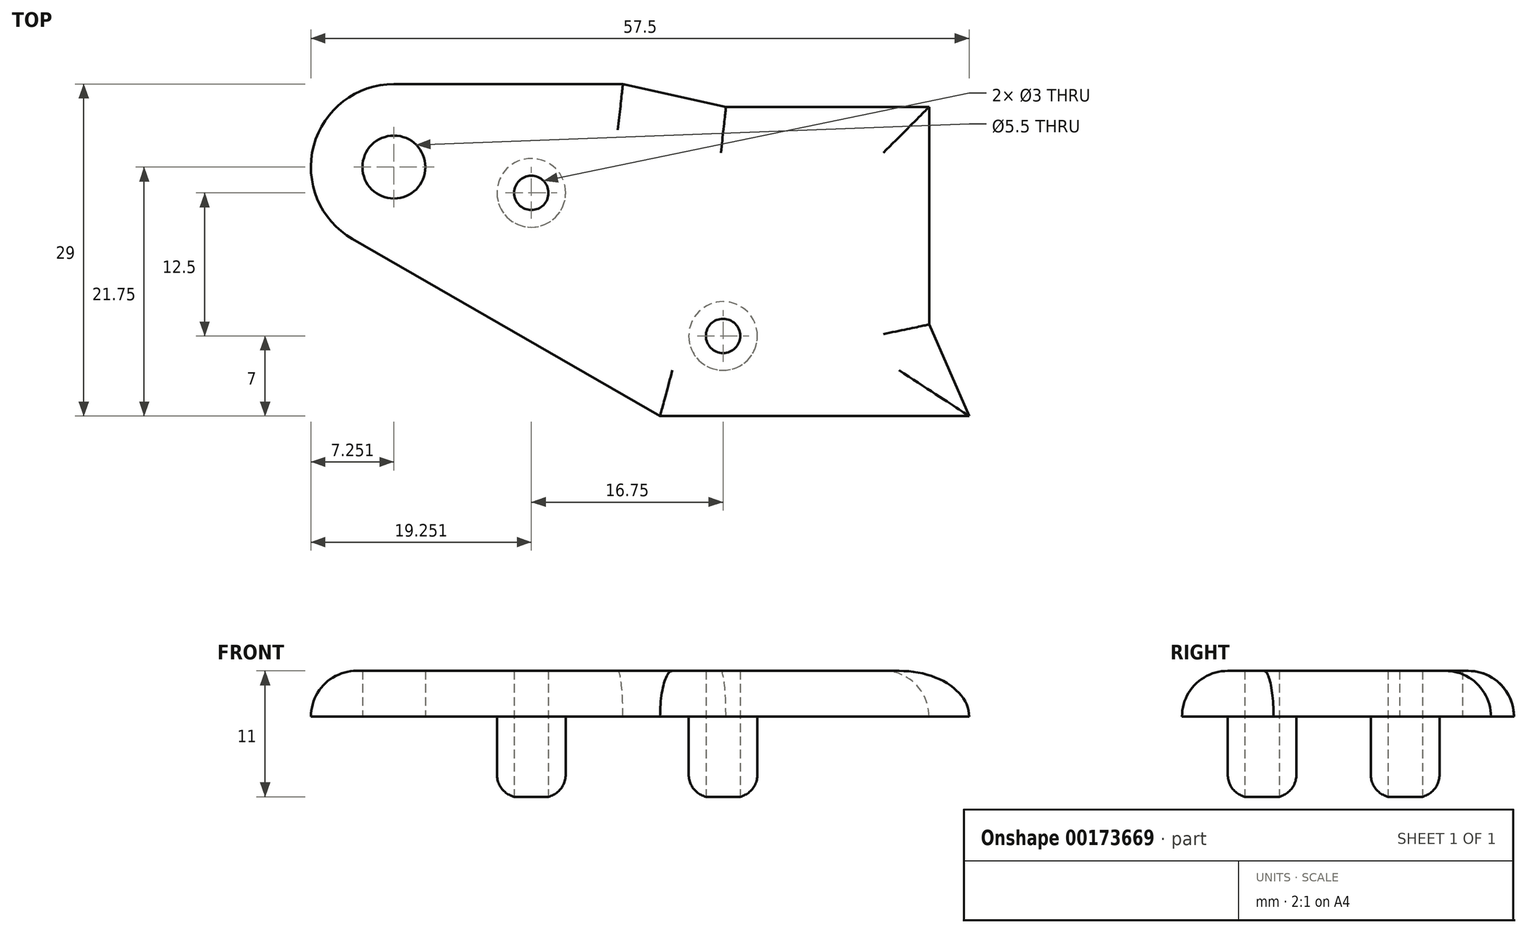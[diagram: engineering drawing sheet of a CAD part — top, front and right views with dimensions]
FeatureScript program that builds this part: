
annotation { "Feature Type Name" : "Feature", "Feature Type Description" : "" }
export const myFeature = defineFeature(function(context is Context, id is Id, definition is map)
    precondition{}
    {
        {
            var Q0;
            Q0=qCreatedBy(makeId("Top.planeOp"),FACE);
            var sketch = newSketch(context, id + "F0", { "sketchPlane" : qUnion([Q0])});
            skLineSegment(sketch, "E0.bottom", {"start": v(23.5, 0) * mm, "end": v(0, 0) * mm});
            skLineSegment(sketch, "E0.top", {"start": v(23.5, 27) * mm, "end": v(5.75, 27) * mm});
            skLineSegment(sketch, "E0.left", {"start": v(23.5, 0) * mm, "end": v(23.5, 27) * mm});
            skLineSegment(sketch, "E0.right", {"start": v(0, 0) * mm, "end": v(0, 27) * mm, "construction": true});
            skLineSegment(sketch, "E1", {"start": v(-23.25, 29) * mm, "end": v(-3.25, 29) * mm});
            skLineSegment(sketch, "E2", {"start": v(0, 0) * mm, "end": v(-26.87, 15.47) * mm});
            skLineSegment(sketch, "E3", {"start": v(-3.25, 29) * mm, "end": v(5.75, 27) * mm});
            skLineSegment(sketch, "E4", {"start": v(23.5, 0) * mm, "end": v(27, 0) * mm});
            skLineSegment(sketch, "E5", {"start": v(27, 0) * mm, "end": v(23.5, 8) * mm});
            skArc(sketch, "E6", {"start": v(-23.25, 29) * mm, "mid": v(-30.25, 23.62) * mm, "end": v(-26.87, 15.47) * mm});
            skArc(sketch, "E7", {"start": v(-26.87, 15.47) * mm, "mid": v(-16.24, 19.88) * mm, "end": v(-23.25, 29) * mm, "construction": true});
            skLineSegment(sketch, "E8", {"start": v(5.75, 27) * mm, "end": v(0, 27) * mm, "construction": true});
            skCircle(sketch, "E9", {"center": v(-23.25, 21.75) * mm, "radius": 2.75 * mm});
            skLineSegment(sketch, "E10.bottom", {"start": v(-23.25, 21.75) * mm, "end": v(-11.25, 21.75) * mm, "construction": true});
            skLineSegment(sketch, "E10.top", {"start": v(-23.25, 19.5) * mm, "end": v(-11.25, 19.5) * mm, "construction": true});
            skLineSegment(sketch, "E10.left", {"start": v(-23.25, 21.75) * mm, "end": v(-23.25, 19.5) * mm, "construction": true});
            skLineSegment(sketch, "E10.right", {"start": v(-11.25, 21.75) * mm, "end": v(-11.25, 19.5) * mm, "construction": true});
            skCircle(sketch, "E11", {"center": v(-11.25, 19.5) * mm, "radius": 3 * mm});
            skCircle(sketch, "E12", {"center": v(-11.25, 19.5) * mm, "radius": 1.5 * mm});
            skLineSegment(sketch, "E13", {"start": v(5.5, 0) * mm, "end": v(5.5, 7) * mm, "construction": true});
            skCircle(sketch, "E14", {"center": v(5.5, 7) * mm, "radius": 1.5 * mm});
            skCircle(sketch, "E15", {"center": v(5.5, 7) * mm, "radius": 3 * mm});
            skSolve(sketch);
        }
        {
            var Q0;
            {var subQ0=sQuery(id+"F0.wireOp",EDGE,"E0.bottom");Q0=makeQuery(id+"F0.imprint","IMPRINT",FACE,{"disambiguationData":[TD([[makeQuery(id+"F0.imprint","IMPRINT",EDGE,{"derivedFrom":subQ0}),-1.0]])]});}
            var Q1;
            {var subQ0=sQuery(id+"F0.wireOp",EDGE,"E4");Q1=makeQuery(id+"F0.imprint","IMPRINT",FACE,{"disambiguationData":[TD([[makeQuery(id+"F0.imprint","IMPRINT",EDGE,{"derivedFrom":subQ0}),1.0]])]});}
            var Q2;
            Q2=makeQuery(id+"F0.imprint","IMPRINT",FACE,{"disambiguationData":[TD([[makeQuery(id+"F0.imprint","IMPRINT",EDGE,{"derivedFrom":sQuery(id+"F0.wireOp",EDGE,"E11")}),1.0]])]});
            var Q3;
            Q3=makeQuery(id+"F0.imprint","IMPRINT",FACE,{"disambiguationData":[TD([[makeQuery(id+"F0.imprint","IMPRINT",EDGE,{"derivedFrom":sQuery(id+"F0.wireOp",EDGE,"E14")}),-1.0]])]});
            extrude(context, id + "F1", {"entities" : qUnion([Q0, Q1, Q2, Q3]), "depth" : 4 * mm});
        }
        {
            var Q0;
            Q0=makeQuery(id+"F0.imprint","IMPRINT",FACE,{"disambiguationData":[TD([[makeQuery(id+"F0.imprint","IMPRINT",EDGE,{"derivedFrom":sQuery(id+"F0.wireOp",EDGE,"E11")}),1.0]])]});
            var Q1;
            Q1=makeQuery(id+"F0.imprint","IMPRINT",FACE,{"disambiguationData":[TD([[makeQuery(id+"F0.imprint","IMPRINT",EDGE,{"derivedFrom":sQuery(id+"F0.wireOp",EDGE,"E14")}),-1.0]])]});
            var Q2;
            Q2=sQuery(id+"F0.wireOp",EDGE,"E15");
            extrude(context, id + "F2", {"entities" : qUnion([Q0, Q1]), "operationType" : NewBodyOperationType.ADD, "surfaceEntities" : qUnion([Q2]), "oppositeDirection" : true, "depth" : 7 * mm});
        }
        {
            var Q0;
            Q0=makeQuery(id+"F2.opExtrude","CAP_EDGE",EDGE,{"disambiguationData":[OSD([sQuery(id+"F0.wireOp",EDGE,"E11")])],"isStart":false});
            var Q1;
            Q1=makeQuery(id+"F2.opExtrude","CAP_EDGE",EDGE,{"disambiguationData":[OSD([sQuery(id+"F0.wireOp",EDGE,"E15")])],"isStart":false});
            fillet(context, id + "F3", {"entities" : qUnion([Q0, Q1]), "radius" : 2 * mm, "tangentPropagation" : true, "allowEdgeOverflow" : false});
        }
        {
            var Q0;
            Q0=makeQuery(id+"F1.opExtrude","CAP_EDGE",EDGE,{"disambiguationData":[OSD([sQuery(id+"F0.wireOp",EDGE,"E1")])],"isStart":false});
            var Q1;
            Q1=makeQuery(id+"F1.opExtrude","CAP_EDGE",EDGE,{"disambiguationData":[OSD([sQuery(id+"F0.wireOp",EDGE,"E0.bottom"),sQuery(id+"F0.wireOp",EDGE,"E4")])],"isStart":false});
            var Q2;
            Q2=makeQuery(id+"F1.opExtrude","CAP_EDGE",EDGE,{"disambiguationData":[OSD([sQuery(id+"F0.wireOp",EDGE,"E5")])],"isStart":false});
            var Q3;
            Q3=makeQuery(id+"F1.opExtrude","CAP_EDGE",EDGE,{"disambiguationData":[OSD([sQuery(id+"F0.wireOp",EDGE,"E0.left")])],"isStart":false});
            var Q4;
            Q4=makeQuery(id+"F1.opExtrude","CAP_EDGE",EDGE,{"disambiguationData":[OSD([sQuery(id+"F0.wireOp",EDGE,"E3")])],"isStart":false});
            var Q5;
            Q5=makeQuery(id+"F1.opExtrude","CAP_EDGE",EDGE,{"disambiguationData":[OSD([sQuery(id+"F0.wireOp",EDGE,"E0.top")])],"isStart":false});
            fillet(context, id + "F4", {"entities" : qUnion([Q0, Q1, Q2, Q3, Q4, Q5]), "radius" : 4 * mm, "tangentPropagation" : true, "allowEdgeOverflow" : false});
        }
    });
